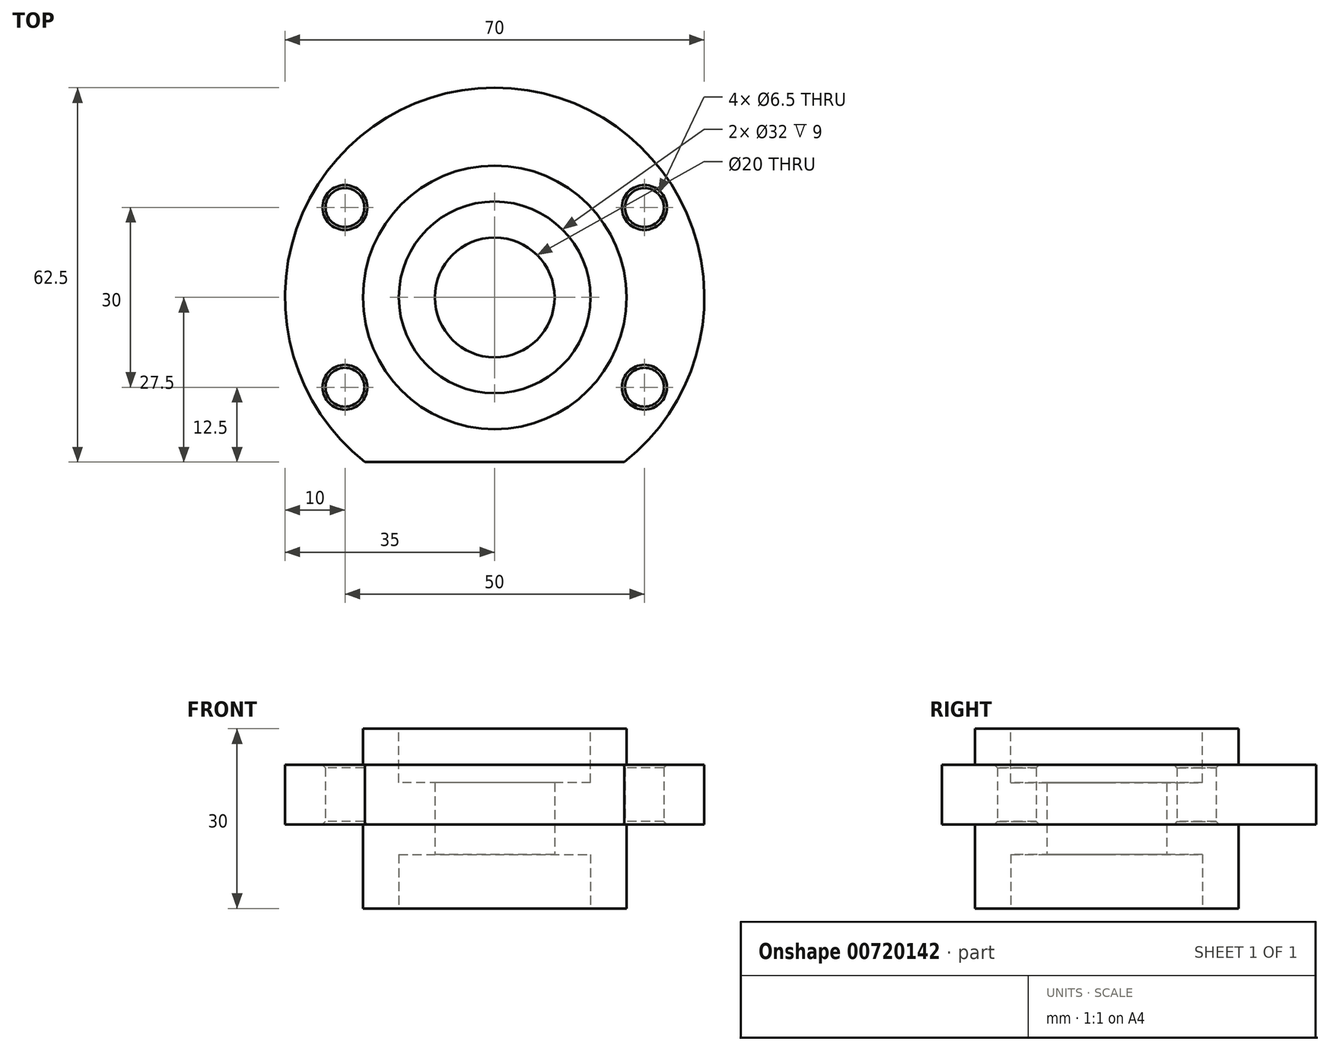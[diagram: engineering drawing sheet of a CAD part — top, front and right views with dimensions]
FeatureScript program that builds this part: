
annotation { "Feature Type Name" : "Feature", "Feature Type Description" : "" }
export const myFeature = defineFeature(function(context is Context, id is Id, definition is map)
    precondition{}
    {
        {
            var Q0;
            Q0=qCreatedBy(makeId("Top.planeOp"),FACE);
            var sketch = newSketch(context, id + "F0", { "sketchPlane" : qUnion([Q0])});
            skArc(sketch, "E0", {"start": v(21.65, -27.5) * mm, "mid": v(0, 35) * mm, "end": v(-21.65, -27.5) * mm});
            skCircle(sketch, "E1", {"center": v(-25, 15) * mm, "radius": 3.25 * mm});
            skCircle(sketch, "E2.MirrorC", {"center": v(25, 15) * mm, "radius": 3.25 * mm});
            skCircle(sketch, "E3.MirrorC", {"center": v(-25, -15) * mm, "radius": 3.25 * mm});
            skCircle(sketch, "E4.MirrorC", {"center": v(25, -15) * mm, "radius": 3.25 * mm});
            skCircle(sketch, "E5", {"center": v(0, 0) * mm, "radius": 10 * mm});
            skLineSegment(sketch, "E6.0", {"start": v(-21.65, -27.5) * mm, "end": v(21.65, -27.5) * mm});
            skSolve(sketch);
        }
        {
            var Q0;
            Q0=makeQuery(id+"F0.imprint","IMPRINT",FACE,{"disambiguationData":[TD([[makeQuery(id+"F0.imprint","IMPRINT",EDGE,{"derivedFrom":sQuery(id+"F0.wireOp",EDGE,"E0")}),1.0]])]});
            extrude(context, id + "F1", {"entities" : qUnion([Q0]), "depth" : 10 * mm, "offsetDistance" : 25 * mm});
        }
        {
            var Q0;
            Q0=makeQuery(id+"F1.opExtrude","CAP_FACE",FACE,{"disambiguationData":[OSD([sQuery(id+"F0.wireOp",EDGE,"E0"),sQuery(id+"F0.wireOp",EDGE,"E1"),sQuery(id+"F0.wireOp",EDGE,"E2.MirrorC"),sQuery(id+"F0.wireOp",EDGE,"E3.MirrorC"),sQuery(id+"F0.wireOp",EDGE,"E4.MirrorC"),sQuery(id+"F0.wireOp",EDGE,"E5"),sQuery(id+"F0.wireOp",EDGE,"E6.0")])],"isStart":false});
            var sketch = newSketch(context, id + "F2", { "sketchPlane" : qUnion([Q0])});
            skCircle(sketch, "E7", {"center": v(0, 0) * mm, "radius": 22 * mm});
            skSolve(sketch);
        }
        {
            var Q0;
            Q0=makeQuery(id+"F2.imprint","IMPRINT",FACE,{"disambiguationData":[TD([[makeQuery(id+"F2.imprint","IMPRINT",EDGE,{"derivedFrom":sQuery(id+"F2.wireOp",EDGE,"E7")}),1.0]])]});
            extrude(context, id + "F3", {"entities" : qUnion([Q0]), "operationType" : NewBodyOperationType.ADD, "depth" : 6 * mm, "offsetDistance" : 25 * mm});
        }
        {
            var Q0;
            Q0=makeQuery(id+"F3.opExtrude","CAP_FACE",FACE,{"disambiguationData":[OSD([sQuery(id+"F0.wireOp",EDGE,"E5"),sQuery(id+"F2.wireOp",EDGE,"E7")])],"isStart":false});
            var sketch = newSketch(context, id + "F4", { "sketchPlane" : qUnion([Q0])});
            skCircle(sketch, "E8", {"center": v(0, 0) * mm, "radius": 16 * mm});
            skSolve(sketch);
        }
        {
            var Q0;
            Q0=makeQuery(id+"F4.imprint","IMPRINT",FACE,{"disambiguationData":[TD([[makeQuery(id+"F4.imprint","IMPRINT",EDGE,{"derivedFrom":sQuery(id+"F4.wireOp",EDGE,"E8")}),1.0]])]});
            extrude(context, id + "F5", {"entities" : qUnion([Q0]), "operationType" : NewBodyOperationType.REMOVE, "oppositeDirection" : true, "depth" : 9 * mm, "offsetDistance" : 25 * mm});
        }
        {
            var Q0;
            Q0=makeQuery(id+"F1.opExtrude","CAP_FACE",FACE,{"disambiguationData":[OSD([sQuery(id+"F0.wireOp",EDGE,"E0"),sQuery(id+"F0.wireOp",EDGE,"E1"),sQuery(id+"F0.wireOp",EDGE,"E2.MirrorC"),sQuery(id+"F0.wireOp",EDGE,"E3.MirrorC"),sQuery(id+"F0.wireOp",EDGE,"E4.MirrorC"),sQuery(id+"F0.wireOp",EDGE,"E5"),sQuery(id+"F0.wireOp",EDGE,"E6.0")])],"isStart":true});
            var sketch = newSketch(context, id + "F6", { "sketchPlane" : qUnion([Q0])});
            skCircle(sketch, "E9", {"center": v(0, 0) * mm, "radius": 22 * mm});
            skSolve(sketch);
        }
        {
            var Q0;
            Q0=makeQuery(id+"F6.imprint","IMPRINT",FACE,{"disambiguationData":[TD([[makeQuery(id+"F6.imprint","IMPRINT",EDGE,{"derivedFrom":sQuery(id+"F6.wireOp",EDGE,"E9")}),1.0]])]});
            extrude(context, id + "F7", {"entities" : qUnion([Q0]), "operationType" : NewBodyOperationType.ADD, "depth" : 14 * mm, "offsetDistance" : 25 * mm});
        }
        {
            var Q0;
            Q0=makeQuery(id+"F7.opExtrude","CAP_FACE",FACE,{"disambiguationData":[OSD([sQuery(id+"F0.wireOp",EDGE,"E5"),sQuery(id+"F6.wireOp",EDGE,"E9")])],"isStart":false});
            var sketch = newSketch(context, id + "F8", { "sketchPlane" : qUnion([Q0])});
            skCircle(sketch, "E10", {"center": v(0, 0) * mm, "radius": 16 * mm});
            skSolve(sketch);
        }
        {
            var Q0;
            Q0=makeQuery(id+"F8.imprint","IMPRINT",FACE,{"disambiguationData":[TD([[makeQuery(id+"F8.imprint","IMPRINT",EDGE,{"derivedFrom":sQuery(id+"F8.wireOp",EDGE,"E10")}),1.0]])]});
            extrude(context, id + "F9", {"entities" : qUnion([Q0]), "operationType" : NewBodyOperationType.REMOVE, "oppositeDirection" : true, "depth" : 9 * mm, "offsetDistance" : 25 * mm});
        }
        {
            var Q0;
            Q0=makeQuery(id+"F1.opExtrude","CAP_EDGE",EDGE,{"disambiguationData":[OSD([sQuery(id+"F0.wireOp",EDGE,"E3.MirrorC")])],"isStart":false});
            var Q1;
            Q1=makeQuery(id+"F1.opExtrude","CAP_EDGE",EDGE,{"disambiguationData":[OSD([sQuery(id+"F0.wireOp",EDGE,"E1")])],"isStart":false});
            var Q2;
            Q2=makeQuery(id+"F1.opExtrude","CAP_EDGE",EDGE,{"disambiguationData":[OSD([sQuery(id+"F0.wireOp",EDGE,"E2.MirrorC")])],"isStart":false});
            var Q3;
            Q3=makeQuery(id+"F1.opExtrude","CAP_EDGE",EDGE,{"disambiguationData":[OSD([sQuery(id+"F0.wireOp",EDGE,"E4.MirrorC")])],"isStart":false});
            var Q4;
            Q4=makeQuery(id+"F1.opExtrude","CAP_EDGE",EDGE,{"disambiguationData":[OSD([sQuery(id+"F0.wireOp",EDGE,"E2.MirrorC")])],"isStart":true});
            var Q5;
            Q5=makeQuery(id+"F1.opExtrude","CAP_EDGE",EDGE,{"disambiguationData":[OSD([sQuery(id+"F0.wireOp",EDGE,"E4.MirrorC")])],"isStart":true});
            var Q6;
            Q6=makeQuery(id+"F1.opExtrude","CAP_EDGE",EDGE,{"disambiguationData":[OSD([sQuery(id+"F0.wireOp",EDGE,"E1")])],"isStart":true});
            var Q7;
            Q7=makeQuery(id+"F1.opExtrude","CAP_EDGE",EDGE,{"disambiguationData":[OSD([sQuery(id+"F0.wireOp",EDGE,"E3.MirrorC")])],"isStart":true});
            chamfer(context, id + "F10", {"entities" : qUnion([Q0, Q1, Q2, Q3, Q4, Q5, Q6, Q7]), "width" : .5 * mm, "tangentPropagation" : true});
        }
    });
